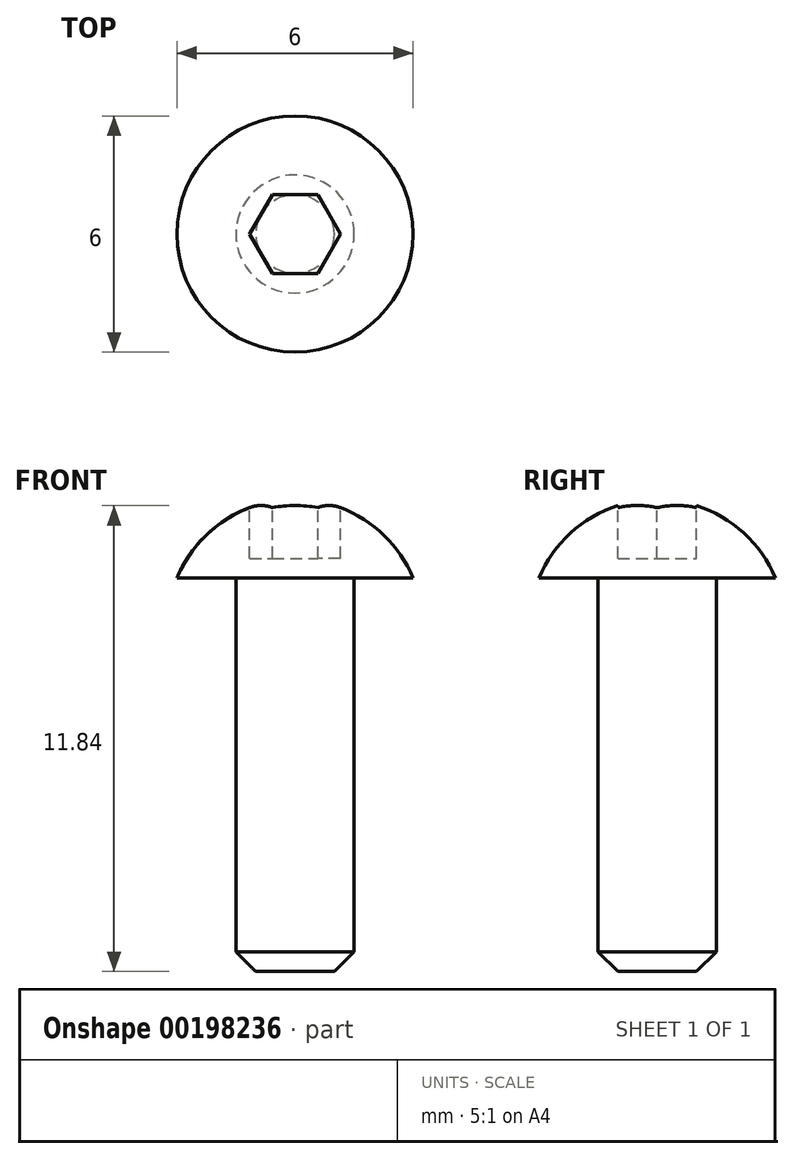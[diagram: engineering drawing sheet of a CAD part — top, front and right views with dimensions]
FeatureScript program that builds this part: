
annotation { "Feature Type Name" : "Feature", "Feature Type Description" : "" }
export const myFeature = defineFeature(function(context is Context, id is Id, definition is map)
    precondition{}
    {
        {
            var Q0;
            Q0=qCreatedBy(makeId("Front.planeOp"),FACE);
            var sketch = newSketch(context, id + "F0", { "sketchPlane" : qUnion([Q0])});
            skLineSegment(sketch, "E0", {"start": v(0, 0) * mm, "end": v(0, 12) * mm});
            skLineSegment(sketch, "E1", {"start": v(0, 0) * mm, "end": v(1.5, 0) * mm});
            skLineSegment(sketch, "E2", {"start": v(1.5, 0) * mm, "end": v(1.5, 10) * mm});
            skLineSegment(sketch, "E3", {"start": v(1.5, 10) * mm, "end": v(3, 10) * mm});
            skArc(sketch, "E4", {"start": v(3, 10) * mm, "mid": v(1.8, 11.45) * mm, "end": v(0, 12) * mm});
            skSolve(sketch);
        }
        {
            var Q0;
            Q0 = qSketchRegion(id + "F0", true);
            var Q1;
            Q1=sQuery(id+"F0.wireOp",EDGE,"E0");
            revolve(context, id + "F1", {"entities" : qUnion([Q0]), "axis" : qUnion([Q1]), "revolveType" : RevolveType.FULL});
        }
        {
            var Q0;
            Q0=makeQuery(id+"F1.opRevolve","SWEPT_EDGE",EDGE,{"disambiguationData":[OSD([sQuery(id+"F0.wireOp",EDGE,"E1"),sQuery(id+"F0.wireOp",EDGE,"E2")])]});
            chamfer(context, id + "F2", {"entities" : qUnion([Q0]), "width" : 0.5 * mm, "tangentPropagation" : true});
        }
        {
            var Q0;
            Q0=qCreatedBy(makeId("Top.planeOp"),FACE);
            cPlane(context, id + "F3", {"entities" : qUnion([Q0]), "cplaneType" : CPlaneType.OFFSET, "offset" : 12 * mm, "width" : 150 * mm, "height" : 150 * mm});
        }
        {
            var Q0;
            Q0=qCreatedBy(id+"F3.planeOp",FACE);
            var sketch = newSketch(context, id + "F4", { "sketchPlane" : qUnion([Q0])});
            skCircle(sketch, "E5.cCircle", {"center": v(0, 0) * mm, "radius": 1 * mm, "construction": true});
            skLineSegment(sketch, "E5.0", {"start": v(-0.58, 1) * mm, "end": v(0.58, 1) * mm});
            skLineSegment(sketch, "E5.1", {"start": v(0.58, 1) * mm, "end": v(1.15, 0) * mm});
            skLineSegment(sketch, "E5.2", {"start": v(1.15, 0) * mm, "end": v(0.58, -1) * mm});
            skLineSegment(sketch, "E5.3", {"start": v(0.58, -1) * mm, "end": v(-0.58, -1) * mm});
            skLineSegment(sketch, "E5.4", {"start": v(-0.58, -1) * mm, "end": v(-1.15, 0) * mm});
            skLineSegment(sketch, "E5.5", {"start": v(-1.15, 0) * mm, "end": v(-0.58, 1) * mm});
            skPoint(sketch, "E5.0.midPoint", {"position": v(0, 1) * mm});
            skSolve(sketch);
        }
        {
            var Q0;
            Q0 = qSketchRegion(id + "F4", true);
            extrude(context, id + "F5", {"entities" : qUnion([Q0]), "operationType" : NewBodyOperationType.REMOVE, "oppositeDirection" : true, "depth" : 1.5 * mm});
        }
    });
